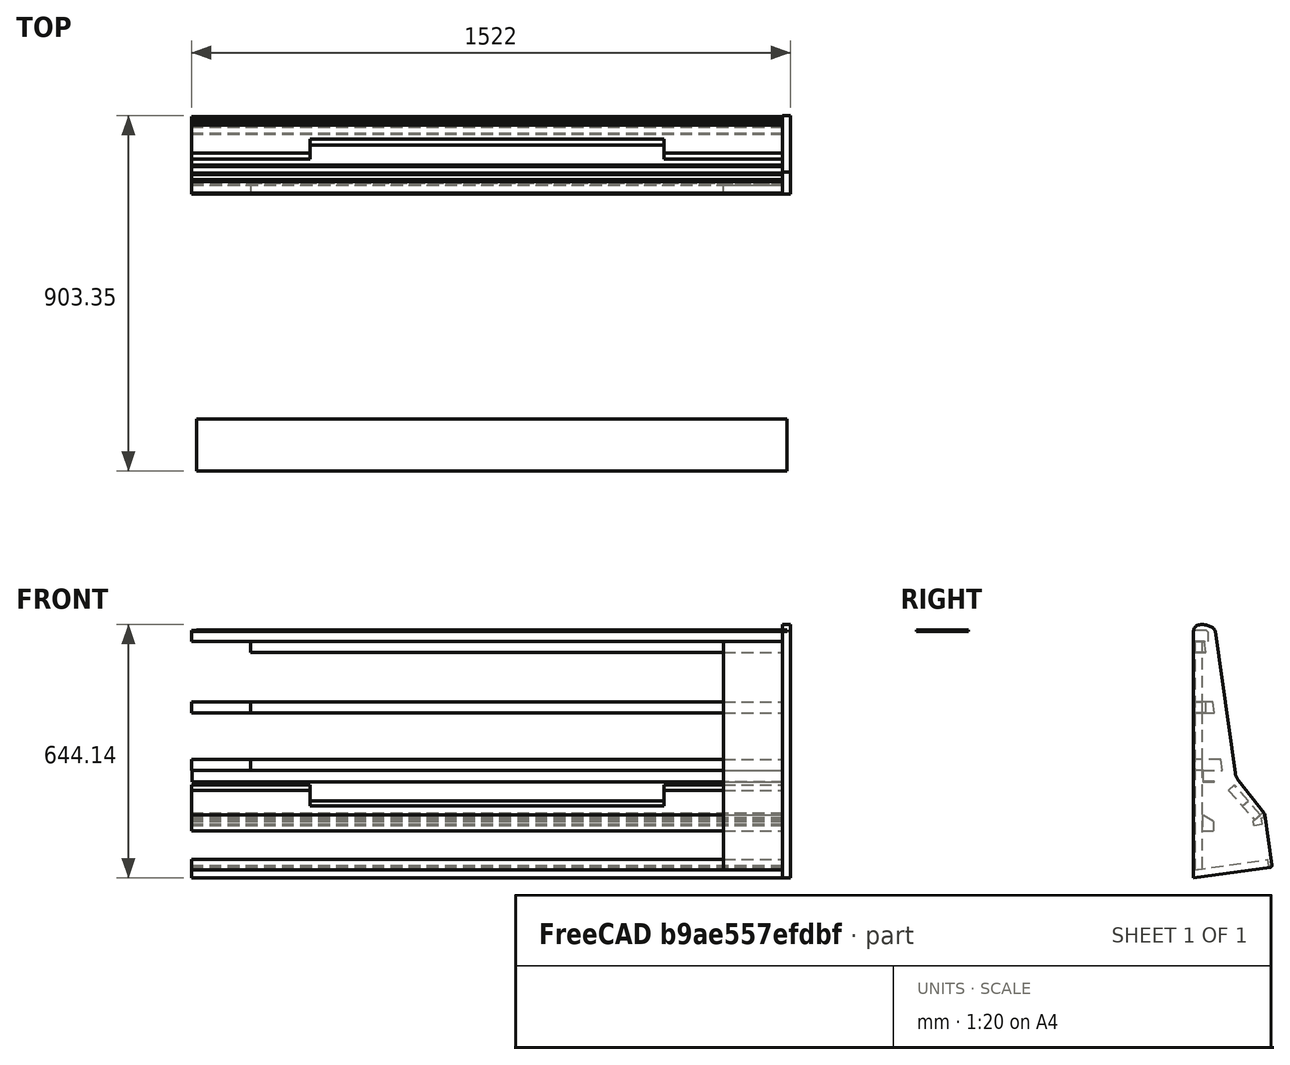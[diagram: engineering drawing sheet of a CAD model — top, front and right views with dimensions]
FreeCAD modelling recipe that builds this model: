
FCSTD DOCUMENT  (FreeCAD 1.0R39109 (Git))
Label: Assemblage_Bati
License: All rights reserved
LicenseURL: http://en.wikipedia.org/wiki/All_rights_reserved
objects: Sketcher::SketchObject×16, PartDesign::Body×14, PartDesign::Pad×12, TechDraw::DrawViewDimension×9, App::Part×6, App::Link×5, PartDesign::CoordinateSystem×4, PartDesign::Pocket×4, PartDesign::FeatureBase×2, TechDraw::DrawProjGroupItem×2, TechDraw::DrawSVGTemplate×1, TechDraw::DrawProjGroup×1, TechDraw::DrawPage×1
note: 117 computed .brp shape members not serialized (recipe doc carries the construction recipe); baked Part::Feature solids carry a one-line shape summary decoded from their .brp
EXTERNAL_REF file=Pieds_REI-acier-57.FCStd obj=Part
EXTERNAL_REF file=ZoneJeu.FCStd obj=ZoneJeu001
EXTERNAL_REF file=StairvilleTriLED.FCStd obj=Part
EXTERNAL_REF file=HT-X8500.FCStd obj=Part

FEATURE [PartDesign::CoordinateSystem] LCS_Origin
  AttacherType = Attacher::AttachEngine3D
  AttachmentSupport = -> [X_Axis]
  MapMode = 2
FEATURE [App::Link] Pied
  LinkPlacement = pos=(0,0,0) rot=(0,1,0;1.5708rad)
  LinkedObject = -> <external Pieds_REI-acier-57.FCStd>#Part
  Placement = pos=(0,0,0) rot=(0,1,0;1.5708rad)
FEATURE [App::Link] Pied001
  LinkPlacement = pos=(1417,-0.000169754,-0.00013578) rot=(0,1,0;1.5708rad)
  LinkedObject = -> <external Pieds_REI-acier-57.FCStd>#Part
  Placement = pos=(1417,-0.000169754,-0.00013578) rot=(0,1,0;1.5708rad)
FEATURE [App::Part] Pieds
  Group = -> [LCS_Origin,Pied,Pied001]
  Origin = -> Origin
  Placement = pos=(331.5,766.5,-360.5) rot=(1,0,0;1.5708rad)
FEATURE [PartDesign::CoordinateSystem] LCS_Origin001
  AttacherType = Attacher::AttachEngine3D
  AttachmentSupport = -> [X_Axis001]
  MapMode = 2
FEATURE [App::Link] ZoneJeu
  LinkPlacement = pos=(737,24.9997,164.302) rot=(0.57735,-0.57735,-0.57735;4.18879rad)
  LinkedObject = -> <external ZoneJeu.FCStd>#ZoneJeu001
  Placement = pos=(737,24.9997,164.302) rot=(0.57735,-0.57735,-0.57735;4.18879rad)
FEATURE [App::Part] TableJeu
  Group = -> [LCS_Origin001,ZoneJeu]
  Origin = -> Origin001
  Placement = pos=(302.5,1093.08,421.726) rot=(1,0,0;1.71042rad)
FEATURE [Sketcher::SketchObject] Sketch001
  ArcFitTolerance = 1e-06
  AttachmentSupport = -> [YZ_Plane004]
  FullyConstrained = true
  MakeInternals = false
  MapMode = 5
  Placement = pos=(0,0,0) rot=(0.57735,0.57735,0.57735;2.0944rad)
  sketch-geometry (6):
    g0: LineSegment StartX=0 StartY=0 StartZ=0 EndX=36 EndY=0 EndZ=0
    g1: LineSegment StartX=36 StartY=24 StartZ=0 EndX=32 EndY=28 EndZ=0
    g2: LineSegment StartX=32 StartY=28 StartZ=0 EndX=2 EndY=28 EndZ=0
    g3: LineSegment StartX=2 StartY=28 StartZ=0 EndX=0 EndY=26 EndZ=0
    g4: LineSegment StartX=0 StartY=26 StartZ=0 EndX=0 EndY=0 EndZ=0
    g5: LineSegment StartX=36 StartY=24 StartZ=0 EndX=36 EndY=0 EndZ=0
  constraints (17):
    c: Coincident(g-1,g0)
    c: PointOnObject(g0,g-1)
    c: Coincident(g1,g2)
    c: Horizontal(g2)
    c: Coincident(g2,g3)
    c: PointOnObject(g3,g-2)
    c: Coincident(g3,g4)
    c: Coincident(g4,g0)
    c: DistanceX(g0,g0) = 36
    c: Coincident(g5,g1)
    c: Coincident(g5,g0)
    c: Vertical(g5)
    c: DistanceY(g0,g1) = 28
    c: Angle(g1,g5) = 2.35619
    c: Angle(g4,g3) = 2.35619
    c: DistanceX(g2,g2) = 30
    c: DistanceX(g3,g2) = 2
FEATURE [PartDesign::Pad] Pad001
  Direction = (1,0,0)
  Length = 1502
  Length2 = 10
  Placement = pos=(0,0,0) rot=(1,1,1;2.0944rad)
  Profile = -> Sketch001
  ReferenceAxis = -> Sketch001 [N_Axis]
  Refine = true
  Suppressed = false
  Type = 0
FEATURE [PartDesign::Body] Body001  label="Nez"
  AllowCompound = false
  Group = -> [Sketch001,Pad001]
  Origin = -> Origin004
  Placement = pos=(-13.5,704,-26) rot=(0,0,1;0rad)
  Tip = -> Pad001
FEATURE [Sketcher::SketchObject] Sketch004
  ArcFitTolerance = 1e-06
  AttachmentSupport = -> [YZ_Plane006]
  FullyConstrained = true
  MakeInternals = false
  MapMode = 5
  Placement = pos=(0,0,0) rot=(0.57735,0.57735,0.57735;2.0944rad)
  sketch-geometry (4):
    g0: LineSegment StartX=0 StartY=0 StartZ=0 EndX=49.6 EndY=0 EndZ=0
    g1: LineSegment StartX=49.6 StartY=0 StartZ=0 EndX=45.6649 EndY=28 EndZ=0
    g2: LineSegment StartX=45.6649 StartY=28 StartZ=0 EndX=0 EndY=28 EndZ=0
    g3: LineSegment StartX=0 StartY=28 StartZ=0 EndX=0 EndY=0 EndZ=0
  constraints (11):
    c: Coincident(g0,g1)
    c: Coincident(g1,g2)
    c: Coincident(g2,g3)
    c: Coincident(g3,g0)
    c: Horizontal(g0)
    c: Horizontal(g2)
    c: Vertical(g3)
    c: Coincident(g0,g-1)
    c: Angle(g1,g0) = 1.43117
    c: DistanceY(g3,g3) = 28
    c: DistanceX(g0,g0) = 49.6
FEATURE [PartDesign::Pad] Pad003
  Direction = (1,0,0)
  Length = 1502
  Length2 = 10
  Placement = pos=(0,0,0) rot=(1,1,1;2.0944rad)
  Profile = -> Sketch004
  ReferenceAxis = -> Sketch004 [N_Axis]
  Refine = true
  Suppressed = false
  Type = 0
FEATURE [Sketcher::SketchObject] Sketch005
  ArcFitTolerance = 1e-06
  AttachmentSupport = -> [YZ_Plane007]
  FullyConstrained = true
  MakeInternals = false
  MapMode = 5
  Placement = pos=(0,0,0) rot=(0.57735,0.57735,0.57735;2.0944rad)
  sketch-geometry (4):
    g0: LineSegment StartX=0 StartY=0 StartZ=0 EndX=70 EndY=0 EndZ=0
    g1: LineSegment StartX=70 StartY=0 StartZ=0 EndX=66.0649 EndY=28 EndZ=0
    g2: LineSegment StartX=66.0649 StartY=28 StartZ=0 EndX=0 EndY=28 EndZ=0
    g3: LineSegment StartX=0 StartY=28 StartZ=0 EndX=0 EndY=0 EndZ=0
  constraints (11):
    c: Coincident(g0,g1)
    c: Coincident(g1,g2)
    c: Coincident(g2,g3)
    c: Coincident(g3,g0)
    c: Horizontal(g0)
    c: Horizontal(g2)
    c: Vertical(g3)
    c: Coincident(g0,g-1)
    c: Angle(g1,g0) = 1.43117
    c: DistanceY(g3,g3) = 28
    c: DistanceX(g0,g0) = 70
FEATURE [PartDesign::Pad] Pad004
  Direction = (1,0,0)
  Length = 1502
  Length2 = 10
  Placement = pos=(0,0,0) rot=(1,1,1;2.0944rad)
  Profile = -> Sketch005
  ReferenceAxis = -> Sketch005 [N_Axis]
  Refine = true
  Suppressed = false
  Type = 0
FEATURE [PartDesign::CoordinateSystem] LCS_Origin002
  AttacherType = Attacher::AttachEngine3D
  AttachmentSupport = -> [X_Axis008]
  MapMode = 2
FEATURE [App::Link] StairvilleTriLED
  LinkPlacement = pos=(738.001,-0.146821,-0.111189) rot=(0,0.707107,0.707107;3.14159rad)
  LinkedObject = -> <external StairvilleTriLED.FCStd>#Part
  Placement = pos=(738.001,-0.146821,-0.111189) rot=(0,0.707107,0.707107;3.14159rad)
FEATURE [App::Part] BarreLed
  Group = -> [LCS_Origin002,StairvilleTriLED]
  Origin = -> Origin008
  Placement = pos=(302,1331.69,386.751) rot=(1,0,0;1.71042rad)
FEATURE [PartDesign::CoordinateSystem] LCS_Origin003
  AttacherType = Attacher::AttachEngine3D
  AttachmentSupport = -> [X_Axis009]
  MapMode = 2
FEATURE [App::Link] HT_X8500  label="HT-X8500"
  LinkPlacement = pos=(-3.05176e-05,0.958765,1.20201) rot=(1.00707,0,0;0rad)
  LinkedObject = -> <external HT-X8500.FCStd>#Part
  Placement = pos=(-3.05176e-05,0.958765,1.20201) rot=(1.00707,0,0;0rad)
FEATURE [App::Part] BarreSon
  Group = -> [LCS_Origin003,HT_X8500]
  Origin = -> Origin009
  Placement = pos=(594.5,1113.05,406.442) rot=(1,0,0;5.75959rad)
FEATURE [Sketcher::SketchObject] Sketch008
  ArcFitTolerance = 1e-06
  AttachmentSupport = -> [YZ_Plane012]
  FullyConstrained = true
  MakeInternals = false
  MapMode = 5
  Placement = pos=(0,0,0) rot=(0.57735,0.57735,0.57735;2.0944rad)
  sketch-geometry (9):
    g0: LineSegment StartX=0 StartY=-20 StartZ=0 EndX=196.879 EndY=-20 EndZ=0
    g1: LineSegment StartX=199 StartY=-17.8787 StartZ=0 EndX=199 EndY=-16 EndZ=0
    g2: LineSegment StartX=192 StartY=0 StartZ=0 EndX=192 EndY=-16 EndZ=0
    g3: LineSegment StartX=192 StartY=-16 StartZ=0 EndX=199 EndY=-16 EndZ=0
    g4: ArcOfCircle [constr] CenterX=196.879 CenterY=-17.8787 CenterZ=0 NormalX=0 NormalY=0 NormalZ=1 AngleXU=0 Radius=2.12132 StartAngle=4.71239 EndAngle=6.28319
    g5: GeomPoint [constr] X=199 Y=-20 Z=0
    g6: LineSegment StartX=196.879 StartY=-20 StartZ=0 EndX=199 EndY=-17.8787 EndZ=0
    g7: LineSegment StartX=0 StartY=-20 StartZ=0 EndX=2.81082 EndY=-1e-16 EndZ=0
    g8: LineSegment StartX=2.81082 StartY=0 StartZ=0 EndX=192 EndY=0 EndZ=0
  constraints (24):
    c: Vertical(g1)
    c: Horizontal(g0)
    c: Vertical(g2)
    c: Coincident(g3,g2)
    c: Horizontal(g3)
    c: PointOnObject(g5,g1)
    c: PointOnObject(g5,g0)
    c: Tangent(g1,g4) = -1.5708
    c: Tangent(g0,g4) = -1.5708
    c: Coincident(g6,g1)
    c: Coincident(g6,g0)
    c: Coincident(g1,g3)
    c: Distance(g6,g6) = 3
    c: Angle(g0,g7) = 1.43117
    c: Coincident(g8,g7)
    c: PointOnObject(g8,g-1)
    c: Horizontal(g8)
    c: Coincident(g2,g8)
    c: Coincident(g0,g7)
    c: Distance(g2,g2) = 16
    c: DistanceY(g0,g-1) = 20
    c: DistanceX(g0,g1) = 199
    c: PointOnObject(g0,g-2)
    c: Distance(g3,g3) = 7
FEATURE [PartDesign::Pad] Pad006
  Direction = (1,0,0)
  Length = 1502
  Length2 = 10
  Placement = pos=(0,0,0) rot=(1,1,1;2.0944rad)
  Profile = -> Sketch008
  ReferenceAxis = -> Sketch008 [N_Axis]
  Refine = true
  Suppressed = false
  Type = 0
FEATURE [PartDesign::Body] Body007  label="Longeron_arriere"
  AllowCompound = false
  Group = -> [Sketch008,Pad006]
  Origin = -> Origin012
  Placement = pos=(-13.5,701.184,-606.82) rot=(-1,0,0;6.14356rad)
  Tip = -> Pad006
FEATURE [Sketcher::SketchObject] Sketch009
  ArcFitTolerance = 1e-06
  AttachmentSupport = -> [YZ_Plane010]
  FullyConstrained = true
  MakeInternals = false
  MapMode = 5
  Placement = pos=(0,0,0) rot=(0.57735,0.57735,0.57735;2.0944rad)
  sketch-geometry (11):
    g0: LineSegment StartX=0 StartY=0 StartZ=0 EndX=21 EndY=0 EndZ=0
    g1: LineSegment StartX=21 StartY=0 StartZ=0 EndX=21 EndY=16 EndZ=0
    g2: LineSegment StartX=21 StartY=16 StartZ=0 EndX=28 EndY=16 EndZ=0
    g3: LineSegment StartX=28 StartY=16 StartZ=0 EndX=28 EndY=23.8066 EndZ=0
    g4: ArcOfCircle [constr] CenterX=23.4098 CenterY=23.8066 CenterZ=0 NormalX=0 NormalY=0 NormalZ=1 AngleXU=0 Radius=4.5902 StartAngle=0 EndAngle=1.15192
    g5: GeomPoint [constr] X=28 Y=28 Z=0
    g6: LineSegment StartX=28 StartY=23.8066 StartZ=0 EndX=25.2768 EndY=28 EndZ=0
    g7: LineSegment StartX=25.2768 StartY=28 StartZ=0 EndX=-1.7e-15 EndY=11.5851 EndZ=0
    g8: LineSegment StartX=0 StartY=0 StartZ=0 EndX=-1.7e-15 EndY=11.5851 EndZ=0
    g9: LineSegment [constr] StartX=25.2768 StartY=28 StartZ=0 EndX=28 EndY=29.7685 EndZ=0
    g10: LineSegment [constr] StartX=28 StartY=29.7685 StartZ=0 EndX=28 EndY=23.8066 EndZ=0
  constraints (29):
    c: Coincident(g0,g-1)
    c: Horizontal(g0)
    c: Coincident(g1,g0)
    c: Vertical(g1)
    c: Coincident(g2,g1)
    c: Horizontal(g2)
    c: Coincident(g3,g2)
    c: Vertical(g3)
    c: Distance(g2,g2) = 7
    c: Distance(g1,g1) = 16
    c: DistanceY(g0,g5) = 28
    c: PointOnObject(g5,g3)
    c: Tangent(g3,g4) = -1.5708
    c: Coincident(g6,g3)
    c: DistanceX(g0,g2) = 28
    c: PointOnObject(g7,g-2)
    c: Coincident(g8,g0)
    c: Coincident(g8,g7)
    c: Angle(g8,g7) = 2.14675
    c: Coincident(g7,g6)
    c: Coincident(g4,g6)
    c: Coincident(g9,g4)
    c: Coincident(g10,g9)
    c: Coincident(g10,g3)
    c: Vertical(g10)
    c: Parallel(g9,g7)
    c: Distance(g6,g6) = 5
    c: Horizontal(g5,g4)
    c: Perpendicular(g7,g6)
FEATURE [PartDesign::Pad] Pad007
  Direction = (1,0,0)
  Length = 1502
  Length2 = 10
  Placement = pos=(0,0,0) rot=(1,1,1;2.0944rad)
  Profile = -> Sketch009
  ReferenceAxis = -> Sketch009 [N_Axis]
  Refine = true
  Suppressed = false
  Type = 0
FEATURE [PartDesign::Body] Body005  label="Longeron_triangle_avant"
  AllowCompound = false
  Group = -> [Sketch009,Pad007]
  Origin = -> Origin010
  Placement = pos=(-13.5,857.737,-492.817) rot=(1,0,0;0.139626rad)
  Tip = -> Pad007
FEATURE [Sketcher::SketchObject] Sketch010
  ArcFitTolerance = 1e-06
  AttachmentSupport = -> [YZ_Plane013]
  FullyConstrained = true
  MakeInternals = false
  MapMode = 5
  Placement = pos=(0,0,0) rot=(0.57735,0.57735,0.57735;2.0944rad)
  sketch-geometry (6):
    g0: LineSegment StartX=0 StartY=0 StartZ=0 EndX=20 EndY=0 EndZ=0
    g1: LineSegment StartX=20 StartY=0 StartZ=0 EndX=20 EndY=100 EndZ=0
    g2: LineSegment [constr] StartX=20 StartY=100 StartZ=0 EndX=0 EndY=100 EndZ=0
    g3: LineSegment [constr] StartX=0 StartY=100 StartZ=0 EndX=0 EndY=0 EndZ=0
    g4: LineSegment StartX=20 StartY=100 StartZ=0 EndX=0 EndY=100 EndZ=0
    g5: LineSegment StartX=0 StartY=100 StartZ=0 EndX=0 EndY=0 EndZ=0
  constraints (16):
    c: Coincident(g0,g1)
    c: Coincident(g1,g2)
    c: Coincident(g2,g3)
    c: Coincident(g3,g0)
    c: Horizontal(g0)
    c: Horizontal(g2)
    c: Vertical(g1)
    c: Vertical(g3)
    c: Distance(g1,g3) = 20
    c: Distance(g0,g2) = 100
    c: Coincident(g0,g-1)
    c: Coincident(g4,g1)
    c: PointOnObject(g4,g3)
    c: Coincident(g5,g4)
    c: Coincident(g5,g0)
    c: Horizontal(g4)
FEATURE [PartDesign::Pad] Pad008
  Direction = (1,0,0)
  Length = 1502
  Length2 = 10
  Placement = pos=(0,0,0) rot=(1,1,1;2.0944rad)
  Profile = -> Sketch010
  ReferenceAxis = -> Sketch010 [N_Axis]
  Refine = true
  Suppressed = false
  Type = 0
FEATURE [Sketcher::SketchObject] Sketch011
  ArcFitTolerance = 1e-06
  AttachmentSupport = -> [YZ_Plane015]
  FullyConstrained = true
  MakeInternals = false
  MapMode = 5
  Placement = pos=(0,0,0) rot=(0.57735,0.57735,0.57735;2.0944rad)
  sketch-geometry (4):
    g0: LineSegment StartX=0 StartY=0 StartZ=0 EndX=132 EndY=0 EndZ=0
    g1: LineSegment StartX=132 StartY=0 StartZ=0 EndX=132 EndY=3 EndZ=0
    g2: LineSegment StartX=132 StartY=3 StartZ=0 EndX=0 EndY=3 EndZ=0
    g3: LineSegment StartX=0 StartY=3 StartZ=0 EndX=0 EndY=0 EndZ=0
  constraints (11):
    c: Coincident(g0,g1)
    c: Coincident(g1,g2)
    c: Coincident(g2,g3)
    c: Coincident(g3,g0)
    c: Horizontal(g0)
    c: Horizontal(g2)
    c: Vertical(g1)
    c: Vertical(g3)
    c: Coincident(g0,g-1)
    c: Distance(g1,g1) = 3
    c: DistanceX(g2,g2) = 132
FEATURE [PartDesign::Pad] Pad009
  Direction = (1,0,0)
  Length = 1500
  Length2 = 10
  Placement = pos=(0,0,0) rot=(1,1,1;2.0944rad)
  Profile = -> Sketch011
  ReferenceAxis = -> Sketch011 [N_Axis]
  Refine = true
  Suppressed = false
  Type = 0
FEATURE [PartDesign::Body] Body009  label="Cartel"
  AllowCompound = false
  Group = -> [Sketch011,Pad009]
  Origin = -> Origin015
  Tip = -> Pad009
FEATURE [App::Part] Part001  label="Cartel_barre_son"
  Group = -> [Body009]
  Origin = -> Origin014
  Placement = pos=(289.5,1104.54,433.601) rot=(1,0,0;0.715585rad)
FEATURE [Sketcher::SketchObject] Sketch013
  ArcFitTolerance = 1e-06
  AttachmentSupport = -> [YZ_Plane017]
  FullyConstrained = true
  MakeInternals = false
  MapMode = 5
  Placement = pos=(0,0,0) rot=(0.57735,0.57735,0.57735;2.0944rad)
  sketch-geometry (6):
    g0: LineSegment StartX=-3.6e-15 StartY=0 StartZ=0 EndX=28 EndY=0 EndZ=0
    g1: LineSegment [constr] StartX=28 StartY=0 StartZ=0 EndX=28 EndY=40 EndZ=0
    g2: LineSegment [constr] StartX=28 StartY=40 StartZ=0 EndX=-3.6e-15 EndY=40 EndZ=0
    g3: LineSegment StartX=-3.6e-15 StartY=40 StartZ=0 EndX=-3.6e-15 EndY=0 EndZ=0
    g4: LineSegment StartX=28 StartY=23.8342 StartZ=0 EndX=-4.5e-15 EndY=40 EndZ=0
    g5: LineSegment StartX=28 StartY=23.8342 StartZ=0 EndX=28 EndY=0 EndZ=0
  constraints (16):
    c: Coincident(g0,g1)
    c: Coincident(g1,g2)
    c: Coincident(g2,g3)
    c: Coincident(g3,g0)
    c: Horizontal(g0)
    c: Horizontal(g2)
    c: Vertical(g1)
    c: Vertical(g3)
    c: Distance(g1,g3) = 28
    c: Distance(g0,g2) = 40
    c: Coincident(g0,g-1)
    c: PointOnObject(g4,g1)
    c: Coincident(g4,g2)
    c: Angle(g3,g4) = 1.0472
    c: Coincident(g5,g4)
    c: Coincident(g5,g0)
FEATURE [PartDesign::Pad] Pad011
  Direction = (1,0,0)
  Length = 1502
  Length2 = 10
  Placement = pos=(0,0,0) rot=(1,1,1;2.0944rad)
  Profile = -> Sketch013
  ReferenceAxis = -> Sketch013 [N_Axis]
  Refine = true
  Suppressed = false
  Type = 0
FEATURE [PartDesign::Body] Body011  label="Support_barre_son"
  AllowCompound = false
  Group = -> [Sketch013,Pad011]
  Origin = -> Origin017
  Placement = pos=(-13.5,726.949,-506.974) rot=(0,0,1;0rad)
  Tip = -> Pad011
FEATURE [Sketcher::SketchObject] Sketch014
  ArcFitTolerance = 1e-06
  AttachmentSupport = -> [YZ_Plane018]
  FullyConstrained = false
  MakeInternals = false
  MapMode = 5
  Placement = pos=(0,0,0) rot=(0.57735,0.57735,0.57735;2.0944rad)
  sketch-geometry (25):
    g0: LineSegment StartX=0 StartY=0 StartZ=0 EndX=195.049 EndY=27.4123 EndZ=0
    g1: LineSegment StartX=199.304 StartY=33.0596 StartZ=0 EndX=181.481 EndY=159.861 EndZ=0
    g2: LineSegment [constr] StartX=181.108 StartY=162.515 StartZ=0 EndX=107.286 EndY=256.968 EndZ=0
    g3: LineSegment [constr] StartX=107.286 StartY=256.968 StartZ=0 EndX=55.3629 EndY=626.418 EndZ=0
    g4: LineSegment [constr] StartX=52.3921 StartY=629 StartZ=0 EndX=2.12132 EndY=629 EndZ=0
    g5: LineSegment StartX=3.2e-15 StartY=626.879 StartZ=0 EndX=0 EndY=0 EndZ=0
    g6: ArcOfCircle [constr] CenterX=2.12132 CenterY=626.879 CenterZ=0 NormalX=0 NormalY=0 NormalZ=1 AngleXU=0 Radius=2.12132 StartAngle=1.5708 EndAngle=3.14159
    g7: GeomPoint [constr] X=0 Y=629 Z=0
    g8: LineSegment [constr] StartX=2.12132 StartY=629 StartZ=0 EndX=3.1e-15 EndY=626.879 EndZ=0
    g9: ArcOfCircle [constr] CenterX=52.3921 CenterY=626 CenterZ=0 NormalX=0 NormalY=0 NormalZ=1 AngleXU=0 Radius=3 StartAngle=0.139626 EndAngle=1.5708
    g10: GeomPoint [constr] X=55 Y=629 Z=0
    g11-g14: Circle [constr] x4 (B-spline internal-alignment scaffolding for g15; pole/knot coordinates omitted)
    g15: BSplineCurve PolesCount=4 KnotsCount=2 Degree=3 IsPeriodic=0
    g16: GeomPoint [constr] X=3.2e-15 Y=626.879 Z=0
    g17: GeomPoint [constr] X=55.3629 Y=626.418 Z=0
    g18: ArcOfCircle CenterX=145.404 CenterY=273.152 CenterZ=0 NormalX=0 NormalY=0 NormalZ=1 AngleXU=0 Radius=40 StartAngle=3.28122 EndAngle=3.805
    g19: LineSegment StartX=113.888 StartY=248.52 StartZ=0 EndX=179.458 EndY=164.627 EndZ=0
    g20: LineSegment StartX=105.793 StartY=267.586 StartZ=0 EndX=55.3629 EndY=626.418 EndZ=0
    g21: ArcOfCircle CenterX=171.579 CenterY=158.469 CenterZ=0 NormalX=0 NormalY=0 NormalZ=1 AngleXU=0 Radius=10 StartAngle=0.139642 EndAngle=0.663406
    g22: GeomPoint [constr] X=181.108 Y=162.515 Z=0
    g23: ArcOfCircle CenterX=194.353 CenterY=32.3636 CenterZ=0 NormalX=0 NormalY=0 NormalZ=1 AngleXU=0 Radius=5 StartAngle=4.85202 EndAngle=6.42283
    g24: GeomPoint [constr] X=200 Y=28.1082 Z=0
  constraints (49):
    c: Coincident(g0,g-1)
    c: Coincident(g2,g22)
    c: Coincident(g3,g2)
    c: PointOnObject(g7,g-2)
    c: Horizontal(g4)
    c: Coincident(g5,g0)
    c: Angle(g0,g5) = 1.43117
    c: DistanceX(g0,g24) = 200
    c: DistanceX(g7,g10) = 55
    c: DistanceY(g5,g7) = 629
    c: PointOnObject(g7,g4)
    c: PointOnObject(g7,g5)
    c: Tangent(g4,g6) = -1.5708
    c: Tangent(g5,g6) = -1.5708
    c: Coincident(g8,g4)
    c: Coincident(g8,g5)
    c: Distance(g8,g8) = 3
    c: PointOnObject(g10,g4)
    c: PointOnObject(g10,g3)
    c: Tangent(g4,g9) = -1.5708
    c: Tangent(g3,g9) = -1.5708
    c: Angle(g4,g3) = 1.71042
    c: Radius(g9) = 3
    c: Weight(g11) = 1
    c: Equal(g11,g12)
    c: Equal(g11,g13)
    c: Equal(g11,g14)
    c: InternalAlignment(g11-g14 -> g15) x4
    c: InternalAlignment(g16,g15)
    c: InternalAlignment(g17,g15)
    c: Coincident(g11,g5)
    c: Coincident(g14,g3)
    c: Vertical(g12,g15)
    c: Tangent(g18,g2) = 1.5708
    c: Tangent(g18,g3) = 1.5708
    c: Diameter(g18) = 80
    c: Coincident(g19,g18)
    c: Coincident(g20,g18)
    c: Coincident(g20,g15)
    c: PointOnObject(g22,g1)
    c: PointOnObject(g22,g19)
    c: Tangent(g1,g21) = -1.5708
    c: Tangent(g19,g21) = 1.5708
    c: Radius(g21) = 10
    c: PointOnObject(g24,g0)
    c: PointOnObject(g24,g1)
    c: Tangent(g0,g23) = -1.5708
    c: Tangent(g1,g23) = -1.5708
    c: Radius(g23) = 5
FEATURE [PartDesign::Pad] Pad012
  Direction = (1,0,0)
  Length = 20
  Length2 = 10
  Placement = pos=(0,0,0) rot=(1,1,1;2.0944rad)
  Profile = -> Sketch014
  ReferenceAxis = -> Sketch014 [N_Axis]
  Refine = true
  Suppressed = false
  Type = 0
FEATURE [PartDesign::Body] Body012  label="Flanc"
  AllowCompound = false
  Group = -> [Sketch014,Pad012]
  Origin = -> Origin018
  Placement = pos=(-33.4,704,-627) rot=(0,0,1;0rad)
  Tip = -> Pad012
FEATURE [Sketcher::SketchObject] Sketch015
  ArcFitTolerance = 1e-06
  AttachmentSupport = -> [YZ_Plane019]
  FullyConstrained = true
  MakeInternals = false
  MapMode = 5
  Placement = pos=(0,0,0) rot=(0.57735,0.57735,0.57735;2.0944rad)
  sketch-geometry (6):
    g0: LineSegment StartX=0 StartY=0 StartZ=0 EndX=30 EndY=0 EndZ=0
    g1: LineSegment StartX=30 StartY=0 StartZ=0 EndX=30 EndY=1.5 EndZ=0
    g2: LineSegment StartX=30 StartY=1.5 StartZ=0 EndX=1.5 EndY=1.5 EndZ=0
    g3: LineSegment StartX=1.5 StartY=1.5 StartZ=0 EndX=1.5 EndY=30 EndZ=0
    g4: LineSegment StartX=1.5 StartY=30 StartZ=0 EndX=0 EndY=30 EndZ=0
    g5: LineSegment StartX=0 StartY=30 StartZ=0 EndX=0 EndY=0 EndZ=0
  constraints (17):
    c: Distance(g0) = 30
    c: Coincident(g0,g-1)
    c: PointOnObject(g0,g-1)
    c: Distance(g1) = 1.5
    c: Coincident(g1,g0)
    c: Vertical(g1)
    c: Coincident(g2,g1)
    c: Horizontal(g2)
    c: Coincident(g3,g2)
    c: Vertical(g3)
    c: Coincident(g4,g3)
    c: PointOnObject(g4,g-2)
    c: Horizontal(g4)
    c: Coincident(g5,g4)
    c: Coincident(g5,g0)
    c: Equal(g4,g1)
    c: Equal(g0,g5)
FEATURE [PartDesign::Pad] Pad013
  Direction = (1,0,0)
  Length = 1500
  Length2 = 10
  Placement = pos=(0,0,0) rot=(1,1,1;2.0944rad)
  Profile = -> Sketch015
  ReferenceAxis = -> Sketch015 [N_Axis]
  Refine = true
  Suppressed = false
  Type = 0
FEATURE [PartDesign::Body] Body013  label="Corniere_aluminium"
  AllowCompound = false
  Group = -> [Sketch015,Pad013]
  Origin = -> Origin019
  Placement = pos=(-12,727.1,-383) rot=(0,0,1;0rad)
  Tip = -> Pad013
FEATURE [Sketcher::SketchObject] Sketch016
  ArcFitTolerance = 1e-06
  AttachmentSupport = -> [Pad003]
  FullyConstrained = true
  MakeInternals = false
  MapMode = 5
  Placement = pos=(0,0,0) rot=(0.707107,0.707107,0;3.14159rad)
  sketch-geometry (8):
    g0: LineSegment StartX=0 StartY=0 StartZ=0 EndX=28 EndY=0 EndZ=0
    g1: LineSegment StartX=28 StartY=0 StartZ=0 EndX=28 EndY=150 EndZ=0
    g2: LineSegment StartX=28 StartY=150 StartZ=0 EndX=0 EndY=150 EndZ=0
    g3: LineSegment StartX=0 StartY=150 StartZ=0 EndX=0 EndY=0 EndZ=0
    g4: LineSegment StartX=0 StartY=1502 StartZ=0 EndX=0 EndY=1352 EndZ=0
    g5: LineSegment StartX=0 StartY=1352 StartZ=0 EndX=20 EndY=1352 EndZ=0
    g6: LineSegment StartX=20 StartY=1352 StartZ=0 EndX=20 EndY=1502 EndZ=0
    g7: LineSegment StartX=20 StartY=1502 StartZ=0 EndX=0 EndY=1502 EndZ=0
  constraints (23):
    c: Coincident(g0,g1)
    c: Coincident(g1,g2)
    c: Coincident(g2,g3)
    c: Coincident(g3,g0)
    c: Horizontal(g0)
    c: Horizontal(g2)
    c: Vertical(g1)
    c: Vertical(g3)
    c: Coincident(g0,g-1)
    c: DistanceY(g3,g3) = 150
    c: Distance(g2,g2) = 28
    c: Coincident(g4,g5)
    c: Coincident(g5,g6)
    c: Coincident(g6,g7)
    c: Coincident(g7,g4)
    c: Vertical(g4)
    c: Vertical(g6)
    c: Horizontal(g5)
    c: Horizontal(g7)
    c: DistanceY(g4,g4) = 150
    c: Distance(g7,g7) = 20
    c: PointOnObject(g4,g-2)
    c: DistanceY(g0,g4) = 1502
FEATURE [PartDesign::Pocket] Pocket
  BaseFeature = -> Pad003
  Direction = (0,0,1)
  Length = 5
  Length2 = 5
  Placement = pos=(0,0,0) rot=(1,1,1;2.0944rad)
  Profile = -> Sketch016
  ReferenceAxis = -> Sketch016 [N_Axis]
  Refine = true
  Suppressed = false
  Type = 1
FEATURE [PartDesign::Body] Body003  label="Longeron_central_tableJeu"
  AllowCompound = false
  Group = -> [Sketch004,Pad003,Sketch016,Pocket]
  Origin = -> Origin006
  Placement = pos=(-13.5,707,-207.5) rot=(0,0,1;0rad)
  Tip = -> Pocket
FEATURE [Sketcher::SketchObject] Sketch017
  ArcFitTolerance = 1e-06
  AttachmentSupport = -> [Pad004]
  FullyConstrained = true
  MakeInternals = false
  MapMode = 5
  Placement = pos=(0,0,0) rot=(0.707107,0.707107,0;3.14159rad)
  sketch-geometry (8):
    g0: LineSegment StartX=0 StartY=0 StartZ=0 EndX=20 EndY=0 EndZ=0
    g1: LineSegment StartX=20 StartY=0 StartZ=0 EndX=20 EndY=150 EndZ=0
    g2: LineSegment StartX=20 StartY=150 StartZ=0 EndX=0 EndY=150 EndZ=0
    g3: LineSegment StartX=0 StartY=150 StartZ=0 EndX=0 EndY=0 EndZ=0
    g4: LineSegment StartX=0 StartY=1352 StartZ=0 EndX=20 EndY=1352 EndZ=0
    g5: LineSegment StartX=20 StartY=1352 StartZ=0 EndX=20 EndY=1502 EndZ=0
    g6: LineSegment StartX=20 StartY=1502 StartZ=0 EndX=0 EndY=1502 EndZ=0
    g7: LineSegment StartX=0 StartY=1502 StartZ=0 EndX=0 EndY=1352 EndZ=0
  constraints (23):
    c: Coincident(g0,g1)
    c: Coincident(g1,g2)
    c: Coincident(g2,g3)
    c: Coincident(g3,g0)
    c: Horizontal(g0)
    c: Horizontal(g2)
    c: Vertical(g1)
    c: Vertical(g3)
    c: Distance(g0,g0) = 20
    c: DistanceY(g3,g3) = 150
    c: Coincident(g4,g5)
    c: Coincident(g5,g6)
    c: Coincident(g6,g7)
    c: Coincident(g7,g4)
    c: Horizontal(g4)
    c: Horizontal(g6)
    c: Vertical(g5)
    c: Vertical(g7)
    c: Equal(g7,g3)
    c: Equal(g4,g2)
    c: DistanceY(g0,g6) = 1502
    c: Coincident(g0,g-1)
    c: PointOnObject(g6,g-2)
FEATURE [PartDesign::Pocket] Pocket001
  BaseFeature = -> Pad004
  Direction = (0,0,1)
  Length = 5
  Length2 = 5
  Placement = pos=(0,0,0) rot=(1,1,1;2.0944rad)
  Profile = -> Sketch017
  ReferenceAxis = -> Sketch017 [N_Axis]
  Refine = true
  Suppressed = false
  Type = 1
FEATURE [PartDesign::Body] Body004  label="Longeron_arriere_tableJeu"
  AllowCompound = false
  Group = -> [Sketch005,Pad004,Sketch017,Pocket001]
  Origin = -> Origin007
  Placement = pos=(-13.5,707,-353) rot=(0,0,1;0rad)
  Tip = -> Pocket001
FEATURE [Sketcher::SketchObject] Sketch018
  ArcFitTolerance = 1e-06
  AttachmentSupport = -> [YZ_Plane003]
  FullyConstrained = true
  MakeInternals = false
  MapMode = 5
  Placement = pos=(0,0,0) rot=(0.57735,0.57735,0.57735;2.0944rad)
  sketch-geometry (6):
    g0: LineSegment [constr] StartX=0 StartY=0 StartZ=0 EndX=20 EndY=0 EndZ=0
    g1: LineSegment [constr] StartX=20 StartY=0 StartZ=0 EndX=20 EndY=580 EndZ=0
    g2: LineSegment StartX=20 StartY=580 StartZ=0 EndX=0 EndY=580 EndZ=0
    g3: LineSegment StartX=0 StartY=580 StartZ=0 EndX=0 EndY=0 EndZ=0
    g4: LineSegment StartX=0 StartY=0 StartZ=0 EndX=20 EndY=2.81082 EndZ=0
    g5: LineSegment StartX=20 StartY=2.81082 StartZ=0 EndX=20 EndY=580 EndZ=0
  constraints (16):
    c: Coincident(g0,g1)
    c: Coincident(g1,g2)
    c: Coincident(g2,g3)
    c: Coincident(g3,g0)
    c: Horizontal(g0)
    c: Horizontal(g2)
    c: Vertical(g1)
    c: Vertical(g3)
    c: Coincident(g4,g0)
    c: PointOnObject(g4,g1)
    c: Coincident(g5,g4)
    c: Coincident(g5,g1)
    c: Distance(g2,g2) = 20
    c: Angle(g4,g3) = 1.43117
    c: Coincident(g0,g-1)
    c: DistanceY(g3,g3) = 580
FEATURE [PartDesign::Pad] Pad014
  Direction = (1,0,0)
  Length = 150
  Length2 = 10
  Placement = pos=(0,0,0) rot=(1,1,1;2.0944rad)
  Profile = -> Sketch018
  ReferenceAxis = -> Sketch018 [N_Axis]
  Refine = true
  Suppressed = false
  Type = 0
FEATURE [PartDesign::Body] Body  label="Longeron_fixation_pied"
  AllowCompound = false
  Group = -> [Sketch018,Pad014]
  Origin = -> Origin003
  Placement = pos=(-13.5,707,-606) rot=(0,0,1;0rad)
  Tip = -> Pad014
FEATURE [PartDesign::FeatureBase] Clone
  BaseFeature = -> Body
  Placement = pos=(-12.5,707,-606) rot=(0,0,1;0rad)
  Suppressed = false
FEATURE [PartDesign::Body] Body014  label="Longeron_fixation_pied_2"
  AllowCompound = false
  Group = -> [Clone]
  Origin = -> Origin020
  Placement = pos=(1351,0,0) rot=(0,0,1;0rad)
  Tip = -> Clone
FEATURE [PartDesign::FeatureBase] Clone001
  BaseFeature = -> Body012
  Placement = pos=(-40.5,704,-634.8) rot=(0,0,1;0rad)
  Suppressed = false
FEATURE [PartDesign::Body] Body015  label="Flanc_2"
  AllowCompound = false
  Group = -> [Clone001]
  Origin = -> Origin021
  Placement = pos=(1529,0,7.8) rot=(0,0,1;0rad)
  Tip = -> Clone001
FEATURE [Sketcher::SketchObject] Sketch
  ArcFitTolerance = 1e-06
  AttachmentSupport = -> [XZ_Plane013]
  FullyConstrained = true
  MakeInternals = false
  MapMode = 5
  Placement = pos=(0,0,0) rot=(1,0,0;1.5708rad)
  sketch-geometry (4):
    g0: LineSegment StartX=301 StartY=147 StartZ=0 EndX=301 EndY=47 EndZ=0
    g1: LineSegment StartX=301 StartY=47 StartZ=0 EndX=1201 EndY=47 EndZ=0
    g2: LineSegment StartX=1201 StartY=47 StartZ=0 EndX=1201 EndY=147 EndZ=0
    g3: LineSegment StartX=1201 StartY=147 StartZ=0 EndX=301 EndY=147 EndZ=0
  constraints (12):
    c: Coincident(g0,g1)
    c: Coincident(g1,g2)
    c: Coincident(g2,g3)
    c: Coincident(g3,g0)
    c: Vertical(g0)
    c: Vertical(g2)
    c: Horizontal(g1)
    c: Horizontal(g3)
    c: DistanceX(g3,g3) = 900
    c: Distance(g-2,g0) = 301
    c: DistanceY(g-1,g0) = 47
    c: DistanceY(g0,g0) = 100
FEATURE [PartDesign::Pocket] Pocket002
  BaseFeature = -> Pad008
  Direction = (0,1,-2e-16)
  Length = 5
  Length2 = 5
  Placement = pos=(0,0,0) rot=(1,1,1;2.0944rad)
  Profile = -> Sketch
  ReferenceAxis = -> Sketch [N_Axis]
  Refine = true
  Suppressed = false
  Type = 1
FEATURE [PartDesign::Body] Body008  label="Longeron_cartel"
  AllowCompound = false
  Group = -> [Sketch010,Pad008,Sketch,Pocket002]
  Origin = -> Origin013
  Placement = pos=(-13.5,858.569,-479.357) rot=(1,0,0;0.715585rad)
  Tip = -> Pocket002
FEATURE [Sketcher::SketchObject] Sketch019
  ArcFitTolerance = 1e-06
  AttachmentSupport = -> [YZ_Plane022]
  FullyConstrained = true
  MakeInternals = false
  MapMode = 5
  Placement = pos=(0,0,0) rot=(0.57735,0.57735,0.57735;2.0944rad)
  sketch-geometry (4):
    g0: LineSegment StartX=0 StartY=0 StartZ=0 EndX=28 EndY=0 EndZ=0
    g1: LineSegment StartX=28 StartY=0 StartZ=0 EndX=24.0649 EndY=28 EndZ=0
    g2: LineSegment StartX=24.0649 StartY=28 StartZ=0 EndX=0 EndY=28 EndZ=0
    g3: LineSegment StartX=0 StartY=28 StartZ=0 EndX=0 EndY=0 EndZ=0
  constraints (11):
    c: Coincident(g0,g1)
    c: Coincident(g1,g2)
    c: Coincident(g2,g3)
    c: Coincident(g3,g0)
    c: Horizontal(g0)
    c: Horizontal(g2)
    c: Vertical(g3)
    c: Coincident(g0,g-1)
    c: Angle(g1,g0) = 1.43117
    c: DistanceY(g3,g3) = 28
    c: DistanceX(g0,g0) = 28
FEATURE [PartDesign::Pad] Pad015
  Direction = (1,0,0)
  Length = 1502
  Length2 = 10
  Placement = pos=(0,0,0) rot=(1,1,1;2.0944rad)
  Profile = -> Sketch019
  ReferenceAxis = -> Sketch019 [N_Axis]
  Refine = true
  Suppressed = false
  Type = 0
FEATURE [Sketcher::SketchObject] Sketch020
  ArcFitTolerance = 1e-06
  AttachmentSupport = -> [Pad015]
  FullyConstrained = true
  MakeInternals = false
  MapMode = 5
  Placement = pos=(0,0,0) rot=(0.707107,0.707107,0;3.14159rad)
  sketch-geometry (8):
    g0: LineSegment StartX=0 StartY=0 StartZ=0 EndX=28 EndY=0 EndZ=0
    g1: LineSegment StartX=28 StartY=0 StartZ=0 EndX=28 EndY=150 EndZ=0
    g2: LineSegment StartX=28 StartY=150 StartZ=0 EndX=0 EndY=150 EndZ=0
    g3: LineSegment StartX=0 StartY=150 StartZ=0 EndX=0 EndY=0 EndZ=0
    g4: LineSegment StartX=0 StartY=1502 StartZ=0 EndX=0 EndY=1352 EndZ=0
    g5: LineSegment StartX=0 StartY=1352 StartZ=0 EndX=20 EndY=1352 EndZ=0
    g6: LineSegment StartX=20 StartY=1352 StartZ=0 EndX=20 EndY=1502 EndZ=0
    g7: LineSegment StartX=20 StartY=1502 StartZ=0 EndX=0 EndY=1502 EndZ=0
  constraints (23):
    c: Coincident(g0,g1)
    c: Coincident(g1,g2)
    c: Coincident(g2,g3)
    c: Coincident(g3,g0)
    c: Horizontal(g0)
    c: Horizontal(g2)
    c: Vertical(g1)
    c: Vertical(g3)
    c: Coincident(g0,g-1)
    c: DistanceY(g3,g3) = 150
    c: Distance(g2,g2) = 28
    c: Coincident(g4,g5)
    c: Coincident(g5,g6)
    c: Coincident(g6,g7)
    c: Coincident(g7,g4)
    c: Vertical(g4)
    c: Vertical(g6)
    c: Horizontal(g5)
    c: Horizontal(g7)
    c: DistanceY(g4,g4) = 150
    c: Distance(g7,g7) = 20
    c: PointOnObject(g4,g-2)
    c: DistanceY(g0,g4) = 1502
FEATURE [PartDesign::Pocket] Pocket003
  BaseFeature = -> Pad015
  Direction = (0,0,1)
  Length = 5
  Length2 = 5
  Placement = pos=(0,0,0) rot=(1,1,1;2.0944rad)
  Profile = -> Sketch020
  ReferenceAxis = -> Sketch020 [N_Axis]
  Refine = true
  Suppressed = false
  Type = 1
FEATURE [PartDesign::Body] Body016  label="Longeron_frontal"
  AllowCompound = false
  Group = -> [Sketch019,Pad015,Sketch020,Pocket003]
  Origin = -> Origin022
  Placement = pos=(-13.5,707,-54) rot=(0,0,1;0rad)
  Tip = -> Pocket003
FEATURE [App::Part] Part  label="Armature"
  Group = -> [Body,Body001,Body003,Body004,Body005,Body007,Body008,Body011,Body012,Body013,Body014,Body015,Body016]
  Origin = -> Origin002
  Placement = pos=(302,740.5,-355.5) rot=(1,0,0;1.5708rad)
FEATURE [TechDraw::DrawSVGTemplate] Template  label="Modèle"
  Height = 297
  Orientation = 1
  Template = /Applications/FreeCAD.app/Contents/Resources/share/Mod/TechDraw/Templates/A3_Landscape_m52.svg
  Width = 420
FEATURE [TechDraw::DrawProjGroupItem] View  label="Front"
  CoarseView = false
  Direction = (0,-1,0)
  Focus = 100
  HardHidden = false
  IsoCount = 0
  IsoHidden = false
  IsoVisible = false
  LockPosition = true
  Perspective = false
  Rotation = 0
  RotationVector = (1,0,0)
  Scale = 0.125
  ScaleType = 2
  ScrubCount = 0
  SeamHidden = false
  SeamVisible = false
  SmoothHidden = false
  SmoothVisible = true
  Source = -> [Pieds,Part,Part001,TableJeu]
  Type = 0
  X = 0
  XDirection = (1,0,0)
  Y = 0
FEATURE [TechDraw::DrawProjGroupItem] ProjItem  label="Droite"
  CoarseView = false
  Direction = (1,-1e-16,0)
  Focus = 100
  HardHidden = false
  IsoCount = 0
  IsoHidden = false
  IsoVisible = false
  LockPosition = false
  Perspective = false
  Rotation = 0
  RotationVector = (1,0,0)
  Scale = 0.125
  ScaleType = 2
  ScrubCount = 0
  SeamHidden = false
  SeamVisible = false
  SmoothHidden = false
  SmoothVisible = true
  Source = -> [Pieds,Part,Part001,TableJeu]
  Type = 2
  X = -151.628
  XDirection = (1e-16,1,0)
  Y = 0
FEATURE [TechDraw::DrawProjGroup] ProjGroup
  Anchor = -> View
  AutoDistribute = true
  LockPosition = false
  ProjectionType = 0
  Rotation = 0
  Scale = 0.125
  ScaleType = 1
  Source = -> [Pieds,Part,Part001,TableJeu]
  Views = -> [View,ProjItem]
  X = 260.415
  Y = 181.155
  spacingX = 15
  spacingY = 15
FEATURE [TechDraw::DrawViewDimension] Dimension  label="Cote"
  AngleOverride = false
  Arbitrary = false
  ArbitraryTolerances = false
  BoxCorners = (2) [(-96.3688,-56.8125,-1e-07),(96.3688,56.8125,1e-07)]
  EqualTolerance = true
  ExtensionAngle = 0
  FormatSpec = %.2w
  FormatSpecOverTolerance = %+.2w
  FormatSpecUnderTolerance = %+.2w
  Inverted = false
  LineAngle = 0
  LockPosition = false
  MeasureType = 1
  OverTolerance = 0
  References2D = -> [View]
  Rotation = 0
  ScaleType = 0
  TheoreticalExact = false
  Type = 1
  UnderTolerance = 0
  X = 0
  Y = 70.5453
FEATURE [TechDraw::DrawViewDimension] Dimension001  label="Cote001"
  AngleOverride = false
  Arbitrary = false
  ArbitraryTolerances = false
  BoxCorners = (2) [(-96.3688,-56.8125,-1e-07),(96.3688,56.8125,1e-07)]
  EqualTolerance = true
  ExtensionAngle = 0
  FormatSpec = %.2w
  FormatSpecOverTolerance = %+.2w
  FormatSpecUnderTolerance = %+.2w
  Inverted = false
  LineAngle = 0
  LockPosition = false
  MeasureType = 1
  OverTolerance = 0
  References2D = -> [View]
  Rotation = 0
  ScaleType = 0
  TheoreticalExact = false
  Type = 2
  UnderTolerance = 0
  X = 110.007
  Y = 0
FEATURE [TechDraw::DrawViewDimension] Dimension002  label="Cote002"
  AngleOverride = false
  Arbitrary = false
  ArbitraryTolerances = false
  BoxCorners = (2) [(-39.3125,-56.8125,0),(39.3125,56.8125,0)]
  EqualTolerance = true
  ExtensionAngle = 0
  FormatSpec = %.2w
  FormatSpecOverTolerance = %+.2w
  FormatSpecUnderTolerance = %+.2w
  Inverted = false
  LineAngle = 0
  LockPosition = false
  MeasureType = 1
  OverTolerance = 0
  References2D = -> [ProjItem]
  Rotation = 0
  ScaleType = 0
  TheoreticalExact = false
  Type = 1
  UnderTolerance = 0
  X = -3.16001
  Y = 70.3568
FEATURE [TechDraw::DrawViewDimension] Dimension003  label="Cote003"
  AngleOverride = false
  Arbitrary = false
  ArbitraryTolerances = false
  BoxCorners = (2) [(-96.3688,-56.8125,-1e-07),(96.3688,56.8125,1e-07)]
  EqualTolerance = true
  ExtensionAngle = 0
  FormatSpec = %.2w
  FormatSpecOverTolerance = %+.2w
  FormatSpecUnderTolerance = %+.2w
  Inverted = false
  LineAngle = 0
  LockPosition = false
  MeasureType = 1
  OverTolerance = 0
  References2D = -> [View]
  Rotation = 0
  ScaleType = 0
  TheoreticalExact = false
  Type = 0
  UnderTolerance = 0
  X = -50.1996
  Y = -66.7915
FEATURE [TechDraw::DrawViewDimension] Dimension004  label="Cote004"
  AngleOverride = false
  Arbitrary = false
  ArbitraryTolerances = false
  BoxCorners = (2) [(-96.3688,-56.8125,-1e-07),(96.3688,56.8125,1e-07)]
  EqualTolerance = true
  ExtensionAngle = 0
  FormatSpec = %.2w
  FormatSpecOverTolerance = %+.2w
  FormatSpecUnderTolerance = %+.2w
  Inverted = false
  LineAngle = 0
  LockPosition = false
  MeasureType = 1
  OverTolerance = 0
  References2D = -> [View]
  Rotation = 0
  ScaleType = 0
  TheoreticalExact = false
  Type = 0
  UnderTolerance = 0
  X = 0.056288
  Y = 3.99181
FEATURE [TechDraw::DrawViewDimension] Dimension005  label="Cote005"
  AngleOverride = false
  Arbitrary = false
  ArbitraryTolerances = false
  BoxCorners = (2) [(-96.3688,-56.8125,-1e-07),(96.3688,56.8125,1e-07)]
  EqualTolerance = true
  ExtensionAngle = 0
  FormatSpec = %.2w
  FormatSpecOverTolerance = %+.2w
  FormatSpecUnderTolerance = %+.2w
  Inverted = false
  LineAngle = 0
  LockPosition = false
  MeasureType = 1
  OverTolerance = 0
  References2D = -> [View]
  Rotation = 0
  ScaleType = 0
  TheoreticalExact = false
  Type = 0
  UnderTolerance = 0
  X = -87.3651
  Y = 61.7236
FEATURE [TechDraw::DrawViewDimension] Dimension007  label="Cote007"
  AngleOverride = false
  Arbitrary = false
  ArbitraryTolerances = false
  BoxCorners = (2) [(-96.3688,-56.8125,-1e-07),(96.3688,56.8125,1e-07)]
  EqualTolerance = true
  ExtensionAngle = 0
  FormatSpec = %.2w
  FormatSpecOverTolerance = %+.2w
  FormatSpecUnderTolerance = %+.2w
  Inverted = false
  LineAngle = 0
  LockPosition = false
  MeasureType = 1
  OverTolerance = 0
  References2D = -> [View]
  Rotation = 0
  ScaleType = 0
  TheoreticalExact = false
  Type = 0
  UnderTolerance = 0
  X = 103.007
  Y = 44.3125
FEATURE [TechDraw::DrawViewDimension] Dimension008  label="Cote008"
  AngleOverride = false
  Arbitrary = false
  ArbitraryTolerances = false
  BoxCorners = (2) [(-39.3125,-56.8125,0),(39.3125,56.8125,0)]
  EqualTolerance = true
  ExtensionAngle = 0
  FormatSpec = %.2w
  FormatSpecOverTolerance = %+.2w
  FormatSpecUnderTolerance = %+.2w
  Inverted = false
  LineAngle = 0
  LockPosition = false
  MeasureType = 1
  OverTolerance = 0
  References2D = -> [ProjItem]
  Rotation = 0
  ScaleType = 0
  TheoreticalExact = false
  Type = 0
  UnderTolerance = 0
  X = 40.8859
  Y = -12.5
FEATURE [TechDraw::DrawViewDimension] Dimension009  label="Cote009"
  AngleOverride = false
  Arbitrary = false
  ArbitraryTolerances = false
  BoxCorners = (2) [(-39.3125,-56.8125,0),(39.3125,56.8125,0)]
  EqualTolerance = true
  ExtensionAngle = 0
  FormatSpec = %.2w
  FormatSpecOverTolerance = %+.2w
  FormatSpecUnderTolerance = %+.2w
  Inverted = false
  LineAngle = 0
  LockPosition = false
  MeasureType = 1
  OverTolerance = 0
  References2D = -> [ProjItem]
  Rotation = 0
  ScaleType = 0
  TheoreticalExact = false
  Type = 2
  UnderTolerance = 0
  X = -48.0017
  Y = 35.3678
FEATURE [TechDraw::DrawPage] Page  label="Feuille"
  KeepUpdated = true
  NextBalloonIndex = 1
  ProjectionType = 0
  Template = -> Template
  Views = -> [ProjGroup,Dimension,Dimension001,Dimension002,Dimension003,Dimension004,Dimension005,Dimension007,Dimension008,Dimension009]

RESOLVED EXTERNAL PARTS (link-assembly join: the EXTERNAL_REF files above that resolve inside this repo's crawl, each included once):
---- part HT-X8500.FCStd = doc fcstd_3c142dc3e18d ----
FCSTD DOCUMENT  (FreeCAD 1.0R39109 (Git))
Label: HT-X8500
License: All rights reserved
LicenseURL: http://en.wikipedia.org/wiki/All_rights_reserved
objects: Sketcher::SketchObject×2, PartDesign::Fillet×2, PartDesign::Pad×1, PartDesign::Body×1, App::Part×1
note: 14 computed .brp shape members not serialized (recipe doc carries the construction recipe); baked Part::Feature solids carry a one-line shape summary decoded from their .brp

FEATURE [Sketcher::SketchObject] Sketch
  ArcFitTolerance = 1e-06
  AttachmentSupport = -> [YZ_Plane001]
  FullyConstrained = true
  MakeInternals = false
  MapMode = 5
  Placement = pos=(0,0,0) rot=(0.57735,0.57735,0.57735;2.0944rad)
  sketch-geometry (4):
    g0: LineSegment StartX=0 StartY=0 StartZ=0 EndX=95 EndY=0 EndZ=0
    g1: LineSegment StartX=95 StartY=0 StartZ=0 EndX=95 EndY=62 EndZ=0
    g2: LineSegment StartX=95 StartY=62 StartZ=0 EndX=0 EndY=62 EndZ=0
    g3: LineSegment StartX=0 StartY=62 StartZ=0 EndX=0 EndY=0 EndZ=0
  constraints (11):
    c: Coincident(g0,g1)
    c: Coincident(g1,g2)
    c: Coincident(g2,g3)
    c: Coincident(g3,g0)
    c: Horizontal(g0)
    c: Horizontal(g2)
    c: Vertical(g1)
    c: Vertical(g3)
    c: Coincident(g0,g-1)
    c: DistanceY(g1,g1) = 62
    c: DistanceX(g0,g0) = 95
FEATURE [PartDesign::Pad] Pad
  Direction = (1,0,0)
  Length = 890
  Length2 = 10
  Placement = pos=(0,0,0) rot=(1,1,1;2.0944rad)
  Profile = -> Sketch
  ReferenceAxis = -> Sketch [N_Axis]
  Refine = true
  Suppressed = false
  Type = 0
FEATURE [PartDesign::Fillet] Fillet
  Base = -> Pad [Edge11,Edge12,Edge7,Edge6]
  BaseFeature = -> Pad
  Placement = pos=(0,0,0) rot=(1,1,1;2.0944rad)
  Radius = 20
  Refine = true
  SupportTransform = false
  Suppressed = false
  UseAllEdges = false
FEATURE [PartDesign::Fillet] Fillet001
  Base = -> Fillet [Face10]
  BaseFeature = -> Fillet
  Placement = pos=(0,0,0) rot=(1,1,1;2.0944rad)
  Radius = 12
  Refine = true
  SupportTransform = false
  Suppressed = false
  UseAllEdges = false
FEATURE [Sketcher::SketchObject] Sketch001
  ArcFitTolerance = 1e-06
  AttachmentSupport = -> [Fillet001]
  FullyConstrained = true
  MakeInternals = false
  MapMode = 5
  Placement = pos=(2.09e-14,95,0) rot=(0.57735,0.57735,0.57735;4.18879rad)
FEATURE [PartDesign::Body] Body  label="Corps"
  AllowCompound = false
  Group = -> [Sketch,Pad,Fillet,Fillet001,Sketch001]
  Origin = -> Origin001
  Tip = -> Fillet001
FEATURE [App::Part] Part  label="HT-X8500"
  Group = -> [Body]
  Origin = -> Origin
---- part Pieds_REI-acier-57.FCStd = doc fcstd_bb5a6c55ef96 ----
FCSTD DOCUMENT  (FreeCAD 1.0R39109 (Git))
Label: Pieds_REI-acier-57
License: All rights reserved
LicenseURL: http://en.wikipedia.org/wiki/All_rights_reserved
objects: Sketcher::SketchObject×2, PartDesign::Pad×1, PartDesign::Pocket×1, PartDesign::Body×1, App::Part×1
note: 11 computed .brp shape members not serialized (recipe doc carries the construction recipe); baked Part::Feature solids carry a one-line shape summary decoded from their .brp

FEATURE [Sketcher::SketchObject] Sketch
  ArcFitTolerance = 1e-06
  AttachmentSupport = -> [XY_Plane]
  FullyConstrained = true
  MakeInternals = false
  MapMode = 5
  sketch-geometry (20):
    g0: LineSegment StartX=20 StartY=0 StartZ=0 EndX=560 EndY=2.42e-14 EndZ=0
    g1: LineSegment [constr] StartX=533.096 StartY=3 StartZ=0 EndX=46.9043 EndY=3 EndZ=0
    g2: LineSegment [constr] StartX=46.9043 StartY=3 StartZ=0 EndX=290 EndY=337.49 EndZ=0
    g3: LineSegment StartX=20 StartY=0 StartZ=0 EndX=277.638 EndY=354.5 EndZ=0
    g4: LineSegment StartX=44.724 StartY=709 StartZ=0 EndX=290 EndY=371.51 EndZ=0
    g5: LineSegment StartX=290 StartY=371.51 StartZ=0 EndX=535.276 EndY=709 EndZ=0
    g6: LineSegment StartX=302.362 StartY=354.5 StartZ=0 EndX=560 EndY=2.42e-14 EndZ=0
    g7: LineSegment [constr] StartX=533.096 StartY=3 StartZ=0 EndX=290 EndY=337.49 EndZ=0
    g8: LineSegment StartX=302.362 StartY=354.5 StartZ=0 EndX=560 EndY=709 EndZ=0
    g9: LineSegment StartX=277.638 StartY=354.5 StartZ=0 EndX=20 EndY=709 EndZ=0
    g10: LineSegment [constr] StartX=277.638 StartY=354.5 StartZ=0 EndX=290 EndY=371.51 EndZ=0
    g11: LineSegment [constr] StartX=290 StartY=371.51 StartZ=0 EndX=302.362 EndY=354.5 EndZ=0
    g12: LineSegment [constr] StartX=302.362 StartY=354.5 StartZ=0 EndX=290 EndY=337.49 EndZ=0
    g13: LineSegment [constr] StartX=290 StartY=337.49 StartZ=0 EndX=277.638 EndY=354.5 EndZ=0
    g14: LineSegment StartX=20 StartY=709 StartZ=0 EndX=0 EndY=709 EndZ=0
    g15: LineSegment StartX=0 StartY=709 StartZ=0 EndX=0 EndY=712 EndZ=0
    g16: LineSegment StartX=0 StartY=712 StartZ=0 EndX=580 EndY=712 EndZ=0
    g17: LineSegment StartX=535.276 StartY=709 StartZ=0 EndX=44.724 EndY=709 EndZ=0
    g18: LineSegment StartX=560 StartY=709 StartZ=0 EndX=580 EndY=709 EndZ=0
    g19: LineSegment StartX=580 StartY=712 StartZ=0 EndX=580 EndY=709 EndZ=0
  constraints (55):
    c: Distance(g0) = 540
    c: PointOnObject(g15,g-2)
    c: Horizontal(g1)
    c: Coincident(g2,g1)
    c: Coincident(g3,g0)
    c: Coincident(g5,g4)
    c: Coincident(g6,g0)
    c: Coincident(g7,g1)
    c: Coincident(g7,g2)
    c: Parallel(g6,g4)
    c: Parallel(g3,g5)
    c: Distance(g1,g0) = 3
    c: Distance(g2,g6) = 20
    c: Parallel(g7,g6)
    c: Parallel(g3,g2)
    c: Distance(g1,g3) = 20
    c: Coincident(g9,g3)
    c: DistanceX(g15,g9) = 20
    c: Distance(g4,g9) = 20
    c: Parallel(g9,g4)
    c: Distance(g5,g8) = 20
    c: Parallel(g8,g5)
    c: Coincident(g10,g3)
    c: Coincident(g10,g4)
    c: Coincident(g11,g4)
    c: Coincident(g12,g2)
    c: Coincident(g13,g2)
    c: Coincident(g13,g3)
    c: Parallel(g10,g3)
    c: Parallel(g11,g4)
    c: Coincident(g14,g9)
    c: Horizontal(g14)
    c: Coincident(g15,g14)
    c: Horizontal(g16)
    c: Coincident(g17,g5)
    c: Coincident(g17,g4)
    c: Horizontal(g17)
    c: Horizontal(g4,g9)
    c: Coincident(g6,g8)
    c: Coincident(g6,g12)
    c: Coincident(g11,g6)
    c: DistanceX(g16,g16) = 580
    c: DistanceY(g-1,g15) = 712
    c: Vertical(g15)
    c: Coincident(g16,g15)
    c: Tangent(g0,g-1) = -1.5708
    c: DistanceX(g-1,g0) = 20
    c: Coincident(g18,g8)
    c: Horizontal(g18)
    c: Coincident(g19,g16)
    c: Vertical(g19)
    c: Equal(g19,g15)
    c: DistanceY(g19,g19) = 3
    c: Equal(g18,g14)
    c: Coincident(g19,g18)
FEATURE [PartDesign::Pad] Pad
  Direction = (0,0,1)
  Length = 80
  Length2 = 10
  Midplane = true
  Profile = -> Sketch
  ReferenceAxis = -> Sketch [N_Axis]
  Refine = true
  Suppressed = false
  Type = 0
FEATURE [Sketcher::SketchObject] Sketch002
  ArcFitTolerance = 1e-06
  AttachmentOffset = pos=(0,0,-710) rot=(0,0,1;0rad)
  AttachmentSupport = -> [XZ_Plane]
  FullyConstrained = true
  MakeInternals = false
  MapMode = 5
  Placement = pos=(0,710,-1.577e-13) rot=(1,0,0;1.5708rad)
  sketch-geometry (15):
    g0: Circle CenterX=8 CenterY=28 CenterZ=0 NormalX=0 NormalY=0 NormalZ=1 AngleXU=0 Radius=4
    g1: Circle CenterX=290 CenterY=28 CenterZ=0 NormalX=0 NormalY=0 NormalZ=1 AngleXU=0 Radius=4
    g2: Circle CenterX=572 CenterY=28 CenterZ=0 NormalX=0 NormalY=0 NormalZ=1 AngleXU=0 Radius=4
    g3: LineSegment [constr] StartX=290 StartY=28 StartZ=0 EndX=8 EndY=28 EndZ=0
    g4: LineSegment [constr] StartX=290 StartY=28 StartZ=0 EndX=572 EndY=28 EndZ=0
    g5: LineSegment [constr] StartX=572 StartY=28 StartZ=0 EndX=572 EndY=-28 EndZ=0
    g6: LineSegment [constr] StartX=572 StartY=-28 StartZ=0 EndX=290 EndY=-28 EndZ=0
    g7: LineSegment [constr] StartX=290 StartY=-28 StartZ=0 EndX=8 EndY=-28 EndZ=0
    g8: LineSegment [constr] StartX=8 StartY=-28 StartZ=0 EndX=8 EndY=28 EndZ=0
    g9: Circle CenterX=572 CenterY=-28 CenterZ=0 NormalX=0 NormalY=0 NormalZ=1 AngleXU=0 Radius=4
    g10: Circle CenterX=290 CenterY=-28 CenterZ=0 NormalX=0 NormalY=0 NormalZ=1 AngleXU=0 Radius=4
    g11: Circle CenterX=8 CenterY=-28 CenterZ=0 NormalX=0 NormalY=0 NormalZ=1 AngleXU=0 Radius=4
    g12: LineSegment [constr] StartX=0 StartY=0 StartZ=0 EndX=580 EndY=0 EndZ=0
    g13: Circle [constr] CenterX=290 CenterY=28 CenterZ=0 NormalX=0 NormalY=0 NormalZ=1 AngleXU=0 Radius=291.349
    g14: Circle [constr] CenterX=290 CenterY=28 CenterZ=0 NormalX=0 NormalY=0 NormalZ=1 AngleXU=0 Radius=291.349
  constraints (36):
    c: Equal(g0,g1)
    c: Equal(g0,g2)
    c: Diameter(g0) = 8
    c: Horizontal(g3)
    c: DistanceX(g3,g3) = 282
    c: Coincident(g3,g0)
    c: Coincident(g3,g1)
    c: Coincident(g4,g1)
    c: Coincident(g4,g2)
    c: Horizontal(g4)
    c: Coincident(g5,g2)
    c: Coincident(g6,g5)
    c: Horizontal(g6)
    c: Coincident(g7,g6)
    c: Horizontal(g7)
    c: Coincident(g8,g7)
    c: Coincident(g8,g0)
    c: Vertical(g8)
    c: Equal(g7,g6)
    c: Equal(g3,g4)
    c: DistanceY(g8,g8) = 56
    c: Coincident(g9,g5)
    c: Coincident(g10,g6)
    c: Coincident(g11,g7)
    c: Equal(g11,g10)
    c: Equal(g10,g9)
    c: Equal(g9,g1)
    c: Symmetric(g5,g2,g-1)
    c: Coincident(g12,g-1)
    c: PointOnObject(g12,g-1)
    c: DistanceX(g12,g12) = 580
    c: Coincident(g13,g1)
    c: PointOnObject(g12,g13)
    c: Coincident(g14,g1)
    c: PointOnObject(g12,g14)
    c: Equal(g14,g13)
FEATURE [PartDesign::Pocket] Pocket
  BaseFeature = -> Pad
  Direction = (0,1,-2e-16)
  Length = 5
  Length2 = 5
  Offset = 10
  Profile = -> Sketch002
  ReferenceAxis = -> Sketch002 [N_Axis]
  Refine = true
  Suppressed = false
  Type = 4
FEATURE [PartDesign::Body] Body  label="Pied_Body"
  AllowCompound = false
  Group = -> [Sketch,Pad,Sketch002,Pocket]
  Origin = -> Origin
  Tip = -> Pocket
FEATURE [App::Part] Part  label="Pied"
  Group = -> [Body]
  Origin = -> Origin001
---- part StairvilleTriLED.FCStd = doc fcstd_b23849111d8b (89325 chars; too large to inline — full recipe in that document) ----
---- part ZoneJeu.FCStd = doc fcstd_f0a775433505 (67946 chars; too large to inline — full recipe in that document) ----
